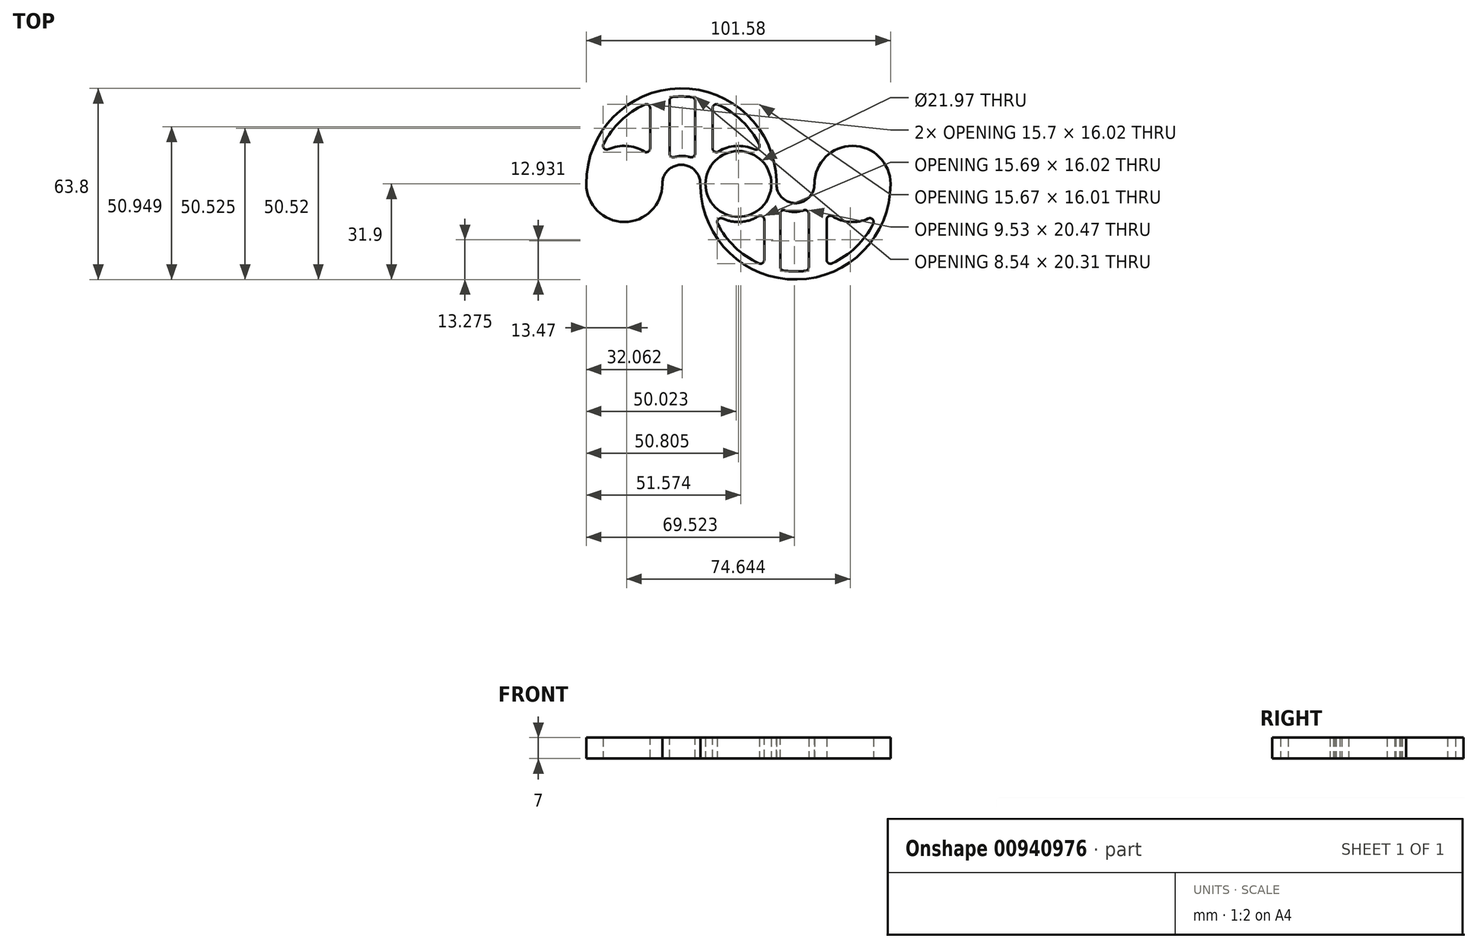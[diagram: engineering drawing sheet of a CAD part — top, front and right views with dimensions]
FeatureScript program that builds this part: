
annotation { "Feature Type Name" : "Feature", "Feature Type Description" : "" }
export const myFeature = defineFeature(function(context is Context, id is Id, definition is map)
    precondition{}
    {
        {
            var Q0;
            Q0=qCreatedBy(makeId("Top.planeOp"),FACE);
            var sketch = newSketch(context, id + "F0", { "sketchPlane" : qUnion([Q0])});
            skCircle(sketch, "E0", {"center": v(-38.08, 0) * mm, "radius": 10.99 * mm});
            skCircle(sketch, "E1", {"center": v(-38.08, 0) * mm, "radius": 12.7 * mm});
            skCircle(sketch, "E2", {"center": v(0, 0) * mm, "radius": 12.7 * mm});
            skArc(sketch, "E3", {"start": v(-12.7, 0) * mm, "mid": v(-19.04, 6.4) * mm, "end": v(-25.38, 0) * mm});
            skArc(sketch, "E4", {"start": v(-11.4, 5.59) * mm, "mid": v(-19.06, 9.33) * mm, "end": v(-26.4, 5.02) * mm});
            skArc(sketch, "E5", {"start": v(12.7, 0) * mm, "mid": v(-19.04, 31.9) * mm, "end": v(-50.78, 0) * mm});
            skArc(sketch, "E6", {"start": v(8.62, 9.33) * mm, "mid": v(-19.04, 29.2) * mm, "end": v(-46.7, 9.33) * mm});
            skPoint(sketch, "E6.startSnap0", {"position": v(-19.06, 9.33) * mm});
            skPoint(sketch, "E6.endSnap0", {"position": v(-19.06, 9.33) * mm});
            skCircle(sketch, "E7", {"center": v(0.02, 0) * mm, "radius": 10.99 * mm});
            skCircle(sketch, "E8", {"center": v(38.1, 0) * mm, "radius": 10.99 * mm});
            skCircle(sketch, "E9", {"center": v(38.1, 0) * mm, "radius": 12.7 * mm});
            skCircle(sketch, "E10", {"center": v(0.02, 0) * mm, "radius": 12.7 * mm});
            skArc(sketch, "E11", {"start": v(12.72, 0) * mm, "mid": v(19.06, -6.4) * mm, "end": v(25.4, 0) * mm});
            skArc(sketch, "E12", {"start": v(11.43, -5.59) * mm, "mid": v(19.08, -9.33) * mm, "end": v(26.43, -5.02) * mm});
            skArc(sketch, "E13", {"start": v(-12.68, 0) * mm, "mid": v(19.06, -31.9) * mm, "end": v(50.8, 0) * mm});
            skArc(sketch, "E14", {"start": v(-8.6, -9.33) * mm, "mid": v(19.06, -29.2) * mm, "end": v(46.72, -9.33) * mm});
            skPoint(sketch, "E14.startSnap0", {"position": v(19.08, -9.33) * mm});
            skPoint(sketch, "E14.endSnap0", {"position": v(19.08, -9.33) * mm});
            skLineSegment(sketch, "E15", {"start": v(29.48, -9.33) * mm, "end": v(29.48, -27.28) * mm});
            skLineSegment(sketch, "E16", {"start": v(8.64, -9.33) * mm, "end": v(8.64, -27.28) * mm});
            skLineSegment(sketch, "E17", {"start": v(-29.46, 9.33) * mm, "end": v(-29.46, 27.28) * mm});
            skLineSegment(sketch, "E18", {"start": v(-8.6, 9.33) * mm, "end": v(-8.6, 27.27) * mm});
            skLineSegment(sketch, "E19", {"start": v(-23, 8.26) * mm, "end": v(-23, 28.94) * mm});
            skLineSegment(sketch, "E20", {"start": v(-14.45, 8.26) * mm, "end": v(-14.45, 28.84) * mm});
            skLineSegment(sketch, "E21", {"start": v(23.5, -7.97) * mm, "end": v(23.5, -28.87) * mm});
            skLineSegment(sketch, "E22", {"start": v(13.98, -7.97) * mm, "end": v(13.98, -28.76) * mm});
            skSolve(sketch);
        }
        {
            var Q0;
            Q0=makeQuery(id+"F0.imprint","IMPRINT",FACE,{"disambiguationData":[TD([[makeQuery(id+"F0.imprint","IMPRINT",EDGE,{"derivedFrom":sQuery(id+"F0.wireOp",EDGE,"E7")}),-1.0]])]});
            var Q1;
            {var subQ0=sQuery(id+"F0.wireOp",EDGE,"E11");Q1=makeQuery(id+"F0.imprint","IMPRINT",FACE,{"disambiguationData":[TD([[makeQuery(id+"F0.imprint","IMPRINT",EDGE,{"derivedFrom":subQ0}),-1.0]])]});}
            var Q2;
            {var subQ0=sQuery(id+"F0.wireOp",EDGE,"E13");var subQ1=sQuery(id+"F0.wireOp",EDGE,"E2");var subQ2=makeQuery(id+"F0.imprint","INTERSECT",VERTEX,{"derivedFrom":[subQ1,subQ0]});Q2=makeQuery(id+"F0.imprint","IMPRINT",FACE,{"disambiguationData":[TD([[makeQuery(id+"F0.imprint","IMPRINT",EDGE,{"disambiguationData":[TD([[subQ2,-1.0]])],"derivedFrom":subQ1}),-1.0]])]});}
            var Q3;
            {var subQ0=sQuery(id+"F0.wireOp",EDGE,"E3");Q3=makeQuery(id+"F0.imprint","IMPRINT",FACE,{"disambiguationData":[TD([[makeQuery(id+"F0.imprint","IMPRINT",EDGE,{"derivedFrom":subQ0}),-1.0]])]});}
            var Q4;
            Q4=makeQuery(id+"F0.imprint","IMPRINT",FACE,{"disambiguationData":[TD([[makeQuery(id+"F0.imprint","IMPRINT",EDGE,{"derivedFrom":sQuery(id+"F0.wireOp",EDGE,"E0")}),-1.0]])]});
            var Q5;
            Q5=makeQuery(id+"F0.imprint","IMPRINT",FACE,{"disambiguationData":[TD([[makeQuery(id+"F0.imprint","IMPRINT",EDGE,{"derivedFrom":sQuery(id+"F0.wireOp",EDGE,"E8")}),-1.0]])]});
            var Q6;
            {var subQ0=sQuery(id+"F0.wireOp",EDGE,"E14");var subQ1=sQuery(id+"F0.wireOp",EDGE,"E2");var subQ2=makeQuery(id+"F0.imprint","INTERSECT",VERTEX,{"derivedFrom":[subQ1,subQ0]});Q6=makeQuery(id+"F0.imprint","IMPRINT",FACE,{"disambiguationData":[TD([[makeQuery(id+"F0.imprint","IMPRINT",EDGE,{"disambiguationData":[TD([[subQ2,-1.0]])],"derivedFrom":subQ1}),1.0]])]});}
            var Q7;
            {var subQ0=sQuery(id+"F0.wireOp",EDGE,"E13");var subQ1=sQuery(id+"F0.wireOp",EDGE,"E2");var subQ2=makeQuery(id+"F0.imprint","INTERSECT",VERTEX,{"derivedFrom":[subQ1,subQ0]});Q7=makeQuery(id+"F0.imprint","IMPRINT",FACE,{"disambiguationData":[TD([[makeQuery(id+"F0.imprint","IMPRINT",EDGE,{"disambiguationData":[TD([[subQ2,-1.0]])],"derivedFrom":subQ1}),1.0]])]});}
            var Q8;
            {var subQ0=sQuery(id+"F0.wireOp",EDGE,"E5");var subQ1=sQuery(id+"F0.wireOp",EDGE,"E2");var subQ2=makeQuery(id+"F0.imprint","INTERSECT",VERTEX,{"derivedFrom":[subQ1,subQ0]});Q8=makeQuery(id+"F0.imprint","IMPRINT",FACE,{"disambiguationData":[TD([[makeQuery(id+"F0.imprint","IMPRINT",EDGE,{"disambiguationData":[TD([[subQ2,-1.0]])],"derivedFrom":subQ1}),-1.0]])]});}
            var Q9;
            {var subQ0=sQuery(id+"F0.wireOp",EDGE,"E6");var subQ1=sQuery(id+"F0.wireOp",EDGE,"E2");var subQ2=makeQuery(id+"F0.imprint","INTERSECT",VERTEX,{"derivedFrom":[subQ1,subQ0]});Q9=makeQuery(id+"F0.imprint","IMPRINT",FACE,{"disambiguationData":[TD([[makeQuery(id+"F0.imprint","IMPRINT",EDGE,{"disambiguationData":[TD([[subQ2,-1.0]])],"derivedFrom":subQ1}),-1.0]])]});}
            var Q10;
            {var subQ0=sQuery(id+"F0.wireOp",EDGE,"E2");var subQ4=makeQuery(id+"F0.imprint","INTERSECT",VERTEX,{"derivedFrom":[subQ0,sQuery(id+"F0.wireOp",EDGE,"E4")]});Q10=makeQuery(id+"F0.imprint","IMPRINT",FACE,{"disambiguationData":[TD([[makeQuery(id+"F0.imprint","IMPRINT",EDGE,{"disambiguationData":[TD([[subQ4,1.0]])],"derivedFrom":subQ0}),1.0]])]});}
            var Q11;
            {var subQ3=sQuery(id+"F0.wireOp",EDGE,"E5");var subQ4=sQuery(id+"F0.wireOp",EDGE,"E2");var subQ5=makeQuery(id+"F0.imprint","INTERSECT",VERTEX,{"derivedFrom":[subQ4,subQ3]});Q11=makeQuery(id+"F0.imprint","IMPRINT",FACE,{"disambiguationData":[TD([[makeQuery(id+"F0.imprint","IMPRINT",EDGE,{"disambiguationData":[TD([[subQ5,1.0]])],"derivedFrom":subQ4}),-1.0]])]});}
            var Q12;
            {var subQ0=sQuery(id+"F0.wireOp",EDGE,"E5");var subQ1=sQuery(id+"F0.wireOp",EDGE,"E1");var subQ2=makeQuery(id+"F0.imprint","INTERSECT",VERTEX,{"derivedFrom":[subQ1,subQ0]});Q12=makeQuery(id+"F0.imprint","IMPRINT",FACE,{"disambiguationData":[TD([[makeQuery(id+"F0.imprint","IMPRINT",EDGE,{"disambiguationData":[TD([[subQ2,1.0]])],"derivedFrom":subQ1}),-1.0]])]});}
            var Q13;
            {var subQ0=sQuery(id+"F0.wireOp",EDGE,"DTZOGkMn-nSdI-sWcP-Samk-YdO5q2ABsoRK");Q13=makeQuery(id+"F0.imprint","IMPRINT",FACE,{"disambiguationData":[TD([[makeQuery(id+"F0.imprint","IMPRINT",EDGE,{"derivedFrom":subQ0}),-1.0]])]});}
            var Q14;
            {var subQ3=sQuery(id+"F0.wireOp",EDGE,"25TYoZCd-IREL-xMh5-7Hmf-XP7vreaXs02i");Q14=makeQuery(id+"F0.imprint","IMPRINT",FACE,{"disambiguationData":[TD([[makeQuery(id+"F0.imprint","IMPRINT",EDGE,{"derivedFrom":subQ3}),-1.0]])]});}
            var Q15;
            {var subQ7=sQuery(id+"F0.wireOp",EDGE,"E20");Q15=makeQuery(id+"F0.imprint","IMPRINT",FACE,{"disambiguationData":[TD([[makeQuery(id+"F0.imprint","IMPRINT",EDGE,{"derivedFrom":subQ7}),-1.0]])]});}
            var Q16;
            {var subQ0=sQuery(id+"F0.wireOp",EDGE,"E17");Q16=makeQuery(id+"F0.imprint","IMPRINT",FACE,{"disambiguationData":[TD([[makeQuery(id+"F0.imprint","IMPRINT",EDGE,{"derivedFrom":subQ0}),-1.0]])]});}
            var Q17;
            {var subQ4=sQuery(id+"F0.wireOp",EDGE,"E16");Q17=makeQuery(id+"F0.imprint","IMPRINT",FACE,{"disambiguationData":[TD([[makeQuery(id+"F0.imprint","IMPRINT",EDGE,{"derivedFrom":subQ4}),1.0]])]});}
            var Q18;
            {var subQ0=sQuery(id+"F0.wireOp",EDGE,"E15");Q18=makeQuery(id+"F0.imprint","IMPRINT",FACE,{"disambiguationData":[TD([[makeQuery(id+"F0.imprint","IMPRINT",EDGE,{"derivedFrom":subQ0}),-1.0]])]});}
            var Q19;
            Q19=makeQuery(id+"F0.imprint","IMPRINT",FACE,{"disambiguationData":[TD([[makeQuery(id+"F0.imprint","IMPRINT",EDGE,{"derivedFrom":sQuery(id+"F0.wireOp",EDGE,"E0")}),1.0]])]});
            var Q20;
            Q20=makeQuery(id+"F0.imprint","IMPRINT",FACE,{"disambiguationData":[TD([[makeQuery(id+"F0.imprint","IMPRINT",EDGE,{"derivedFrom":sQuery(id+"F0.wireOp",EDGE,"E8")}),1.0]])]});
            extrude(context, id + "F1", {"entities" : qUnion([Q0, Q1, Q2, Q3, Q4, Q5, Q6, Q7, Q8, Q9, Q10, Q11, Q12, Q13, Q14, Q15, Q16, Q17, Q18, Q19, Q20]), "depth" : 7 * mm, "offsetDistance" : 25.4 * mm});
        }
        {
            var Q0;
            Q0=makeQuery(id+"F1.opExtrude","SWEPT_EDGE",EDGE,{"disambiguationData":[OSD([sQuery(id+"F0.wireOp",EDGE,"E1"),sQuery(id+"F0.wireOp",EDGE,"E5")])]});
            var Q1;
            Q1=makeQuery(id+"F1.opExtrude","SWEPT_EDGE",EDGE,{"disambiguationData":[OSD([sQuery(id+"F0.wireOp",EDGE,"E2"),sQuery(id+"F0.wireOp",EDGE,"E3")])]});
            var Q2;
            Q2=makeQuery(id+"F1.opExtrude","SWEPT_EDGE",EDGE,{"disambiguationData":[OSD([sQuery(id+"F0.wireOp",EDGE,"E2"),sQuery(id+"F0.wireOp",EDGE,"E13")])]});
            var Q3;
            Q3=makeQuery(id+"F1.opExtrude","SWEPT_EDGE",EDGE,{"disambiguationData":[OSD([sQuery(id+"F0.wireOp",EDGE,"E1"),sQuery(id+"F0.wireOp",EDGE,"E3")])]});
            var Q4;
            {var subQ0=sQuery(id+"F0.wireOp",EDGE,"E10");var subQ1=sQuery(id+"F0.wireOp",EDGE,"E2");Q4=makeQuery(id+"F1.opExtrude","SWEPT_EDGE",EDGE,{"disambiguationData":[OSD([subQ1,subQ0]),TDD([makeQuery(id+"F0.imprint","INTERSECT",VERTEX,{"disambiguationData":[OD(0.0)],"derivedFrom":[subQ1,subQ0]})])]});}
            var Q5;
            Q5=makeQuery(id+"F1.opExtrude","SWEPT_EDGE",EDGE,{"disambiguationData":[OSD([sQuery(id+"F0.wireOp",EDGE,"E5"),sQuery(id+"F0.wireOp",EDGE,"E10")])]});
            var Q6;
            Q6=makeQuery(id+"F1.opExtrude","SWEPT_EDGE",EDGE,{"disambiguationData":[OSD([sQuery(id+"F0.wireOp",EDGE,"E10"),sQuery(id+"F0.wireOp",EDGE,"E11")])]});
            var Q7;
            Q7=makeQuery(id+"F1.opExtrude","SWEPT_EDGE",EDGE,{"disambiguationData":[OSD([sQuery(id+"F0.wireOp",EDGE,"E9"),sQuery(id+"F0.wireOp",EDGE,"E11")])]});
            var Q8;
            Q8=makeQuery(id+"F1.opExtrude","SWEPT_EDGE",EDGE,{"disambiguationData":[OSD([sQuery(id+"F0.wireOp",EDGE,"E9"),sQuery(id+"F0.wireOp",EDGE,"E13")])]});
            var Q9;
            {var subQ0=sQuery(id+"F0.wireOp",EDGE,"E10");var subQ1=sQuery(id+"F0.wireOp",EDGE,"E2");Q9=makeQuery(id+"F1.opExtrude","SWEPT_EDGE",EDGE,{"disambiguationData":[OSD([subQ1,subQ0]),TDD([makeQuery(id+"F0.imprint","INTERSECT",VERTEX,{"disambiguationData":[OD(1.0)],"derivedFrom":[subQ1,subQ0]})])]});}
            fillet(context, id + "F2", {"entities" : qUnion([Q0, Q1, Q2, Q3, Q4, Q5, Q6, Q7, Q8, Q9]), "radius" : 5.08 * mm, "tangentPropagation" : true, "allowEdgeOverflow" : false});
        }
        {
            var Q0;
            Q0=makeQuery(id+"F1.opExtrude","SWEPT_EDGE",EDGE,{"disambiguationData":[OSD([sQuery(id+"F0.wireOp",EDGE,"E14"),sQuery(id+"F0.wireOp",EDGE,"E15")])]});
            var Q1;
            Q1=makeQuery(id+"F1.opExtrude","SWEPT_EDGE",EDGE,{"disambiguationData":[OSD([sQuery(id+"F0.wireOp",EDGE,"E9"),sQuery(id+"F0.wireOp",EDGE,"E15")])]});
            var Q2;
            Q2=makeQuery(id+"F1.opExtrude","SWEPT_EDGE",EDGE,{"disambiguationData":[OSD([sQuery(id+"F0.wireOp",EDGE,"E9"),sQuery(id+"F0.wireOp",EDGE,"E14")])]});
            var Q3;
            Q3=makeQuery(id+"F1.opExtrude","SWEPT_EDGE",EDGE,{"disambiguationData":[OSD([sQuery(id+"F0.wireOp",EDGE,"E12"),sQuery(id+"F0.wireOp",EDGE,"E21")])]});
            var Q4;
            Q4=makeQuery(id+"F1.opExtrude","SWEPT_EDGE",EDGE,{"disambiguationData":[OSD([sQuery(id+"F0.wireOp",EDGE,"E12"),sQuery(id+"F0.wireOp",EDGE,"E22")])]});
            var Q5;
            Q5=makeQuery(id+"F1.opExtrude","SWEPT_EDGE",EDGE,{"disambiguationData":[OSD([sQuery(id+"F0.wireOp",EDGE,"E14"),sQuery(id+"F0.wireOp",EDGE,"E21")])]});
            var Q6;
            Q6=makeQuery(id+"F1.opExtrude","SWEPT_EDGE",EDGE,{"disambiguationData":[OSD([sQuery(id+"F0.wireOp",EDGE,"E14"),sQuery(id+"F0.wireOp",EDGE,"E22")])]});
            var Q7;
            Q7=makeQuery(id+"F1.opExtrude","SWEPT_EDGE",EDGE,{"disambiguationData":[OSD([sQuery(id+"F0.wireOp",EDGE,"E14"),sQuery(id+"F0.wireOp",EDGE,"E16")])]});
            var Q8;
            Q8=makeQuery(id+"F1.opExtrude","SWEPT_EDGE",EDGE,{"disambiguationData":[OSD([sQuery(id+"F0.wireOp",EDGE,"E10"),sQuery(id+"F0.wireOp",EDGE,"E16")])]});
            var Q9;
            Q9=makeQuery(id+"F1.opExtrude","SWEPT_EDGE",EDGE,{"disambiguationData":[OSD([sQuery(id+"F0.wireOp",EDGE,"E2"),sQuery(id+"F0.wireOp",EDGE,"E14")])]});
            var Q10;
            Q10=makeQuery(id+"F1.opExtrude","SWEPT_EDGE",EDGE,{"disambiguationData":[OSD([sQuery(id+"F0.wireOp",EDGE,"E6"),sQuery(id+"F0.wireOp",EDGE,"E19")])]});
            var Q11;
            Q11=makeQuery(id+"F1.opExtrude","SWEPT_EDGE",EDGE,{"disambiguationData":[OSD([sQuery(id+"F0.wireOp",EDGE,"E6"),sQuery(id+"F0.wireOp",EDGE,"E18")])]});
            var Q12;
            Q12=makeQuery(id+"F1.opExtrude","SWEPT_EDGE",EDGE,{"disambiguationData":[OSD([sQuery(id+"F0.wireOp",EDGE,"E6"),sQuery(id+"F0.wireOp",EDGE,"E10")])]});
            var Q13;
            Q13=makeQuery(id+"F1.opExtrude","SWEPT_EDGE",EDGE,{"disambiguationData":[OSD([sQuery(id+"F0.wireOp",EDGE,"E10"),sQuery(id+"F0.wireOp",EDGE,"E18")])]});
            var Q14;
            Q14=makeQuery(id+"F1.opExtrude","SWEPT_EDGE",EDGE,{"disambiguationData":[OSD([sQuery(id+"F0.wireOp",EDGE,"E4"),sQuery(id+"F0.wireOp",EDGE,"E19")])]});
            var Q15;
            Q15=makeQuery(id+"F1.opExtrude","SWEPT_EDGE",EDGE,{"disambiguationData":[OSD([sQuery(id+"F0.wireOp",EDGE,"E4"),sQuery(id+"F0.wireOp",EDGE,"E20")])]});
            var Q16;
            Q16=makeQuery(id+"F1.opExtrude","SWEPT_EDGE",EDGE,{"disambiguationData":[OSD([sQuery(id+"F0.wireOp",EDGE,"E6"),sQuery(id+"F0.wireOp",EDGE,"E20")])]});
            var Q17;
            Q17=makeQuery(id+"F1.opExtrude","SWEPT_EDGE",EDGE,{"disambiguationData":[OSD([sQuery(id+"F0.wireOp",EDGE,"E1"),sQuery(id+"F0.wireOp",EDGE,"E17")])]});
            var Q18;
            Q18=makeQuery(id+"F1.opExtrude","SWEPT_EDGE",EDGE,{"disambiguationData":[OSD([sQuery(id+"F0.wireOp",EDGE,"E6"),sQuery(id+"F0.wireOp",EDGE,"E17")])]});
            var Q19;
            Q19=makeQuery(id+"F1.opExtrude","SWEPT_EDGE",EDGE,{"disambiguationData":[OSD([sQuery(id+"F0.wireOp",EDGE,"E1"),sQuery(id+"F0.wireOp",EDGE,"E6")])]});
            fillet(context, id + "F3", {"entities" : qUnion([Q0, Q1, Q2, Q3, Q4, Q5, Q6, Q7, Q8, Q9, Q10, Q11, Q12, Q13, Q14, Q15, Q16, Q17, Q18, Q19]), "radius" : 1.27 * mm, "tangentPropagation" : true, "allowEdgeOverflow" : false});
        }
    });
